# Revit family: Zumtobel TECTON 2 sensors and controls
name_source: partatom
category: Lighting Devices
units: mm (PartAtom-declared; Revit-internal decimal feet)

## family parameters
Cut with Voids When Loaded = No
Host = Face
Maintain Annotation Orientation = No
Part Type = Normal
Room Calculation Point = Yes
Round Connector Dimension = Use Diameter
Shared = Yes

## types (6) — shared parameters
Assembly Code = Pr_75_75_27_23
Description = Lighting and occupancy sensors
Export Type to IFC As = IfcSensorType
Is HC Type = Yes
Is LC/MC Type = No
Is Only Bluetooth = No
Luminaire Height = 90 mm  [stored 0.295276 ft]
Luminaire Length = 250 mm  [stored 0.82021 ft]
Luminaire Width = 60 mm  [stored 0.19685 ft]
Manufacturer = Zumtobel Lighting
Material Bluetooth = Zumtobel-Plastic-RAL 9005-Jet Black
Material Body = Zumtobel-Plastic-RAL 9003-Signal White
Material Housing = Zumtobel-Plastic-RAL 9003-Signal White
Type IFC Predefined Type = MOVEMENTSENSOR
URL = https://www.zumtobel.com
Visibility B = No
Visibility HC = Yes
Visibility LC/MC = No
Visibility NOT HC = No
zero-valued in all types: Default Elevation

## per-type parameters (varying)
| type | Model | Type Image |
| basicDIM ILD G2 HC TEC2 WH | 22172962 | ZS_TE2_F_MSENS_HC_WH.jpg |
| basicDIM ILD G2 LC TEC2 WH | 22172966 | ZS_TEC_F_MSENS_LC_TEC-GP_WH.jpg |
| basicDIM ILD G2 MC TEC2 WH | 22172961 | ZS_TEC_F_MSENS_LC_TEC-GP_WH.jpg |
| basicDIM ILD G2 HC TEC2 BK | 22173112 | ZS_TE2_F_MSENS_HC_BK.jpg |
| basicDIM ILD G2 LC TEC2 BK | 22173113 | ZS_TEC_F_MSENS_LC_TEC-GP_BK.jpg |
| basicDIM ILD G2 MC TEC2 BK | 22173114 | ZS_TE2_F_MSENS_MC_BK_1.jpg |

note: [stored X ft] marks values corroborated as IEEE doubles in the binary element streams (Revit-internal decimal feet)

## geometry (parser evidence)
native form markers: Sweep x1
no freeform markers — native parametric forms only
